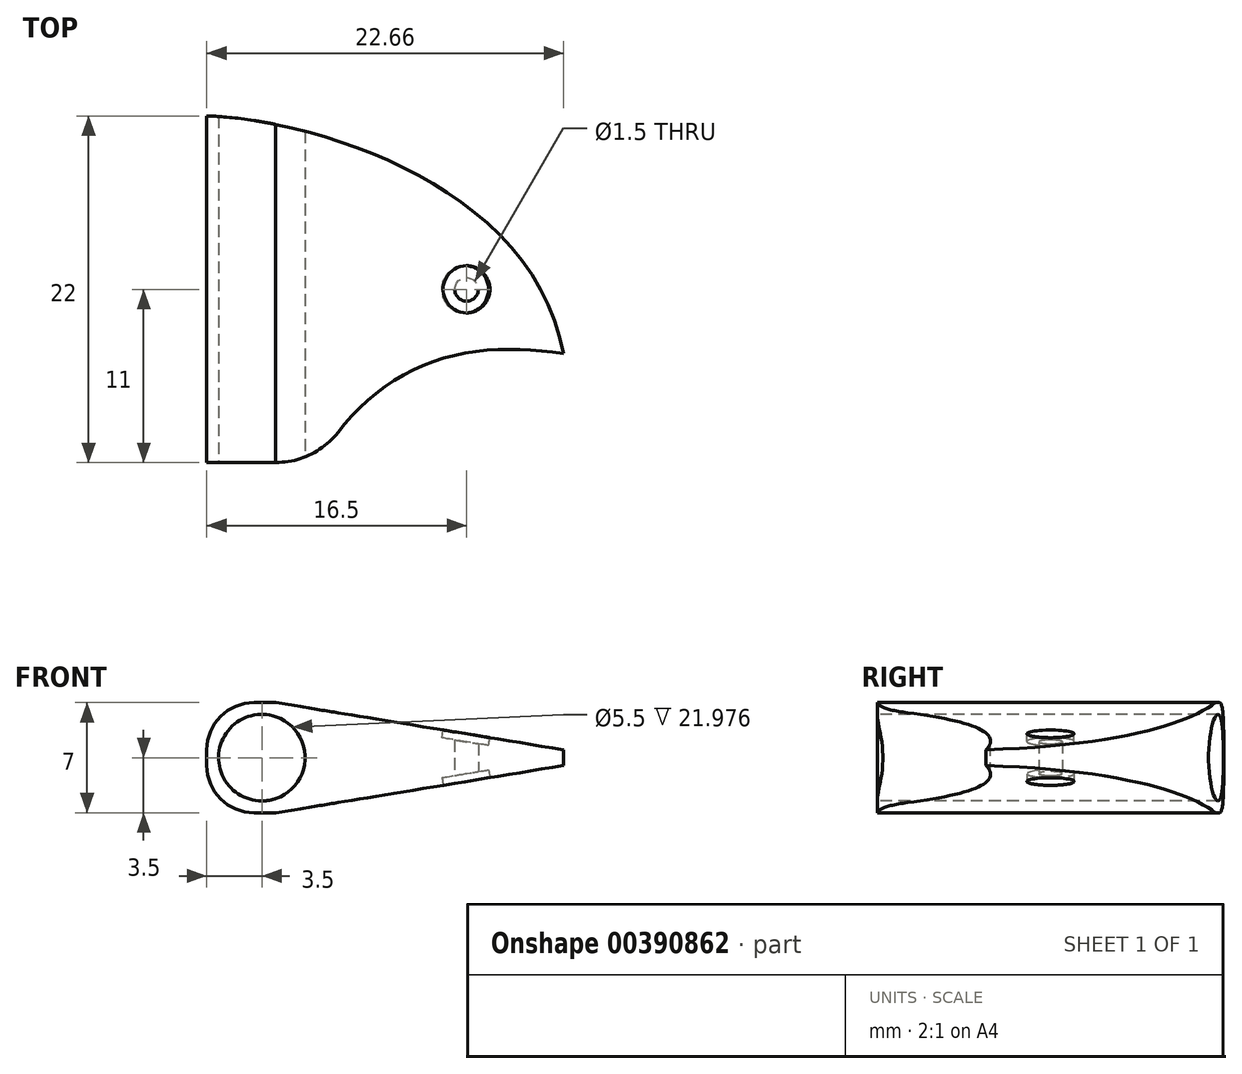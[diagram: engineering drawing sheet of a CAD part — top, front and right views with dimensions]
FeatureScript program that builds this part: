
annotation { "Feature Type Name" : "Feature", "Feature Type Description" : "" }
export const myFeature = defineFeature(function(context is Context, id is Id, definition is map)
    precondition{}
    {
        {
            var Q0;
            Q0=qCreatedBy(makeId("Top.planeOp"),FACE);
            var sketch = newSketch(context, id + "F0", { "sketchPlane" : qUnion([Q0])});
            skLineSegment(sketch, "E0", {"start": v(0, 11) * mm, "end": v(0, -11) * mm});
            skLineSegment(sketch, "E1", {"start": v(0, 0) * mm, "end": v(16.5, 0) * mm, "construction": true});
            skCircle(sketch, "E2", {"center": v(16.5, 0) * mm, "radius": 0.75 * mm});
            skFitSpline(sketch, "E3", {"points": [v(0, 11) * mm, v(22.66, -4.09) * mm], "startDerivative": vector(15.68, -0.07) * mm, "endDerivative": vector(6.42, -34.33) * mm});
            skLineSegment(sketch, "E4", {"start": v(0, -11) * mm, "end": v(7, -11) * mm});
            skFitSpline(sketch, "E5", {"points": [v(7, -11) * mm, v(22.66, -4.09) * mm], "startDerivative": vector(9.8, 15.86) * mm, "endDerivative": vector(23.42, -3.65) * mm});
            skSolve(sketch);
        }
        {
            var Q0;
            Q0=makeQuery(id+"F0.imprint","IMPRINT",FACE,{"disambiguationData":[TD([[makeQuery(id+"F0.imprint","IMPRINT",EDGE,{"derivedFrom":sQuery(id+"F0.wireOp",EDGE,"E0")}),1.0]])]});
            extrude(context, id + "F1", {"entities" : qUnion([Q0]), "depth" : 7 * mm, "offsetDistance" : 25 * mm});
        }
        {
            var Q0;
            Q0=makeQuery(id+"F1.opExtrude","SWEPT_FACE",FACE,{"disambiguationData":[OSD([sQuery(id+"F0.wireOp",EDGE,"E4")])]});
            var sketch = newSketch(context, id + "F2", { "sketchPlane" : qUnion([Q0])});
            skLineSegment(sketch, "E6", {"start": v(0, 0) * mm, "end": v(7, 7) * mm, "construction": true});
            skLineSegment(sketch, "E7", {"start": v(0, 7) * mm, "end": v(7, 0) * mm, "construction": true});
            skCircle(sketch, "E8", {"center": v(3.5, 3.5) * mm, "radius": 2.75 * mm});
            skSolve(sketch);
        }
        {
            var Q0;
            Q0=makeQuery(id+"F2.imprint","IMPRINT",FACE,{"disambiguationData":[TD([[makeQuery(id+"F2.imprint","IMPRINT",EDGE,{"derivedFrom":sQuery(id+"F2.wireOp",EDGE,"E8")}),1.0]])]});
            extrude(context, id + "F3", {"entities" : qUnion([Q0]), "operationType" : NewBodyOperationType.REMOVE, "oppositeDirection" : true, "depth" : 25 * mm, "offsetDistance" : 25 * mm});
        }
        {
            var Q0;
            Q0=makeQuery(id+"F1.opExtrude","CAP_EDGE",EDGE,{"disambiguationData":[OSD([sQuery(id+"F0.wireOp",EDGE,"E0")])],"isStart":true});
            var Q1;
            Q1=makeQuery(id+"F1.opExtrude","CAP_EDGE",EDGE,{"disambiguationData":[OSD([sQuery(id+"F0.wireOp",EDGE,"E0")])],"isStart":false});
            fillet(context, id + "F4", {"entities" : qUnion([Q0, Q1]), "radius" : 3 * mm, "tangentPropagation" : true, "allowEdgeOverflow" : false});
        }
        {
            var Q0;
            Q0=makeQuery(id+"F1.opExtrude","SWEPT_FACE",FACE,{"disambiguationData":[OSD([sQuery(id+"F0.wireOp",EDGE,"E4")])]});
            var sketch = newSketch(context, id + "F5", { "sketchPlane" : qUnion([Q0])});
            skLineSegment(sketch, "E9", {"start": v(7, 7) * mm, "end": v(22.67, 0) * mm, "construction": true});
            skLineSegment(sketch, "E10", {"start": v(22.67, 0) * mm, "end": v(22.67, 7) * mm, "construction": true});
            skLineSegment(sketch, "E11", {"start": v(22.67, 7) * mm, "end": v(7, 0) * mm, "construction": true});
            skLineSegment(sketch, "E12", {"start": v(14.84, 3.5) * mm, "end": v(29.2, 3.5) * mm, "construction": true});
            skLineSegment(sketch, "E13", {"start": v(22.67, 3.5) * mm, "end": v(22.67, 4) * mm});
            skLineSegment(sketch, "E14", {"start": v(22.67, 3.5) * mm, "end": v(22.67, 2.5) * mm});
            skLineSegment(sketch, "E15", {"start": v(26.17, 7.86) * mm, "end": v(22.67, 4) * mm});
            skLineSegment(sketch, "E16", {"start": v(22.67, 4) * mm, "end": v(4.38, 7) * mm});
            skLineSegment(sketch, "E17", {"start": v(4.38, 7) * mm, "end": v(11.56, 11.37) * mm});
            skLineSegment(sketch, "E18", {"start": v(11.56, 11.37) * mm, "end": v(26.17, 7.86) * mm});
            skLineSegment(sketch, "E19.MirrorCS", {"start": v(22.67, 3) * mm, "end": v(4.38, 0) * mm});
            skLineSegment(sketch, "E20.MirrorCS", {"start": v(11.56, -4.37) * mm, "end": v(26.17, -0.86) * mm});
            skLineSegment(sketch, "E21.MirrorCS", {"start": v(4.38, 0) * mm, "end": v(11.56, -4.37) * mm});
            skLineSegment(sketch, "E22.MirrorCS", {"start": v(26.17, -0.86) * mm, "end": v(22.67, 3) * mm});
            skSolve(sketch);
        }
        {
            var Q0;
            {var subQ7=sQuery(id+"F5.wireOp",EDGE,"E15");Q0=makeQuery(id+"F5.imprint","IMPRINT",FACE,{"disambiguationData":[TD([[makeQuery(id+"F5.imprint","IMPRINT",EDGE,{"derivedFrom":subQ7}),-1.0]])]});}
            var Q1;
            Q1=makeQuery(id+"F5.imprint","IMPRINT",FACE,{"disambiguationData":[TD([[makeQuery(id+"F5.imprint","IMPRINT",EDGE,{"derivedFrom":sQuery(id+"F5.wireOp",EDGE,"E20.MirrorCS")}),1.0]])]});
            var Q2;
            {var subQ0=sQuery(id+"F5.wireOp",EDGE,"E16");var subQ1=sQuery(id+"F0.wireOp",EDGE,"E4");var subQ2=makeQuery(id+"F1.opExtrude","CAP_EDGE",EDGE,{"disambiguationData":[OSD([subQ1])],"isStart":false});var subQ3=makeQuery(id+"F5.imprint","INTERSECT",VERTEX,{"derivedFrom":[subQ2,subQ0,sQuery(id+"F5.wireOp",EDGE,"E17")]});Q2=makeQuery(id+"F5.imprint","IMPRINT",FACE,{"disambiguationData":[TD([[makeQuery(id+"F5.imprint","IMPRINT",EDGE,{"disambiguationData":[TD([[subQ3,1.0]])],"derivedFrom":subQ0}),-1.0]])]});}
            var Q3;
            {var subQ0=sQuery(id+"F5.wireOp",EDGE,"E19.MirrorCS");var subQ1=sQuery(id+"F0.wireOp",EDGE,"E4");var subQ2=makeQuery(id+"F1.opExtrude","CAP_EDGE",EDGE,{"disambiguationData":[OSD([subQ1])],"isStart":true});var subQ3=makeQuery(id+"F5.imprint","INTERSECT",VERTEX,{"derivedFrom":[subQ2,subQ0,sQuery(id+"F5.wireOp",EDGE,"E21.MirrorCS")]});Q3=makeQuery(id+"F5.imprint","IMPRINT",FACE,{"disambiguationData":[TD([[makeQuery(id+"F5.imprint","IMPRINT",EDGE,{"disambiguationData":[TD([[subQ3,1.0]])],"derivedFrom":subQ0}),1.0]])]});}
            extrude(context, id + "F6", {"entities" : qUnion([Q0, Q1, Q2, Q3]), "operationType" : NewBodyOperationType.REMOVE, "oppositeDirection" : true, "depth" : 25 * mm, "offsetDistance" : 25 * mm});
        }
        {
            var Q0;
            Q0=makeQuery(id+"F6.boolean.opBoolean","COPY",FACE,{"derivedFrom":makeQuery(id+"F6.opExtrude","SWEPT_FACE",FACE,{"disambiguationData":[OSD([sQuery(id+"F5.wireOp",EDGE,"E16")])]})});
            var sketch = newSketch(context, id + "F7", { "sketchPlane" : qUnion([Q0])});
            skCircle(sketch, "E23", {"center": v(15.47, 0) * mm, "radius": 1.5 * mm});
            skSolve(sketch);
        }
        {
            var Q0;
            Q0 = qSketchRegion(id + "F7", true);
            extrude(context, id + "F8", {"entities" : qUnion([Q0]), "operationType" : NewBodyOperationType.REMOVE, "oppositeDirection" : true, "depth" : .5 * mm, "offsetDistance" : 25 * mm});
        }
        {
            var Q0;
            Q0=makeQuery(id+"F6.boolean.opBoolean","COPY",FACE,{"derivedFrom":makeQuery(id+"F6.opExtrude","SWEPT_FACE",FACE,{"disambiguationData":[OSD([sQuery(id+"F5.wireOp",EDGE,"E19.MirrorCS")])]})});
            var sketch = newSketch(context, id + "F9", { "sketchPlane" : qUnion([Q0])});
            skCircle(sketch, "E24", {"center": v(16.6, 0) * mm, "radius": 1.5 * mm});
            skSolve(sketch);
        }
        {
            var Q0;
            Q0 = qSketchRegion(id + "F9", true);
            extrude(context, id + "F10", {"entities" : qUnion([Q0]), "operationType" : NewBodyOperationType.REMOVE, "oppositeDirection" : true, "depth" : .5 * mm, "offsetDistance" : 25 * mm});
        }
        {
            var Q0;
            Q0=makeQuery(id+"F1.opExtrude","SWEPT_EDGE",EDGE,{"disambiguationData":[OSD([sQuery(id+"F0.wireOp",EDGE,"E4"),sQuery(id+"F0.wireOp",EDGE,"E5")])]});
            fillet(context, id + "F11", {"entities" : qUnion([Q0]), "radius" : 5 * mm, "tangentPropagation" : true, "allowEdgeOverflow" : false});
        }
    });
